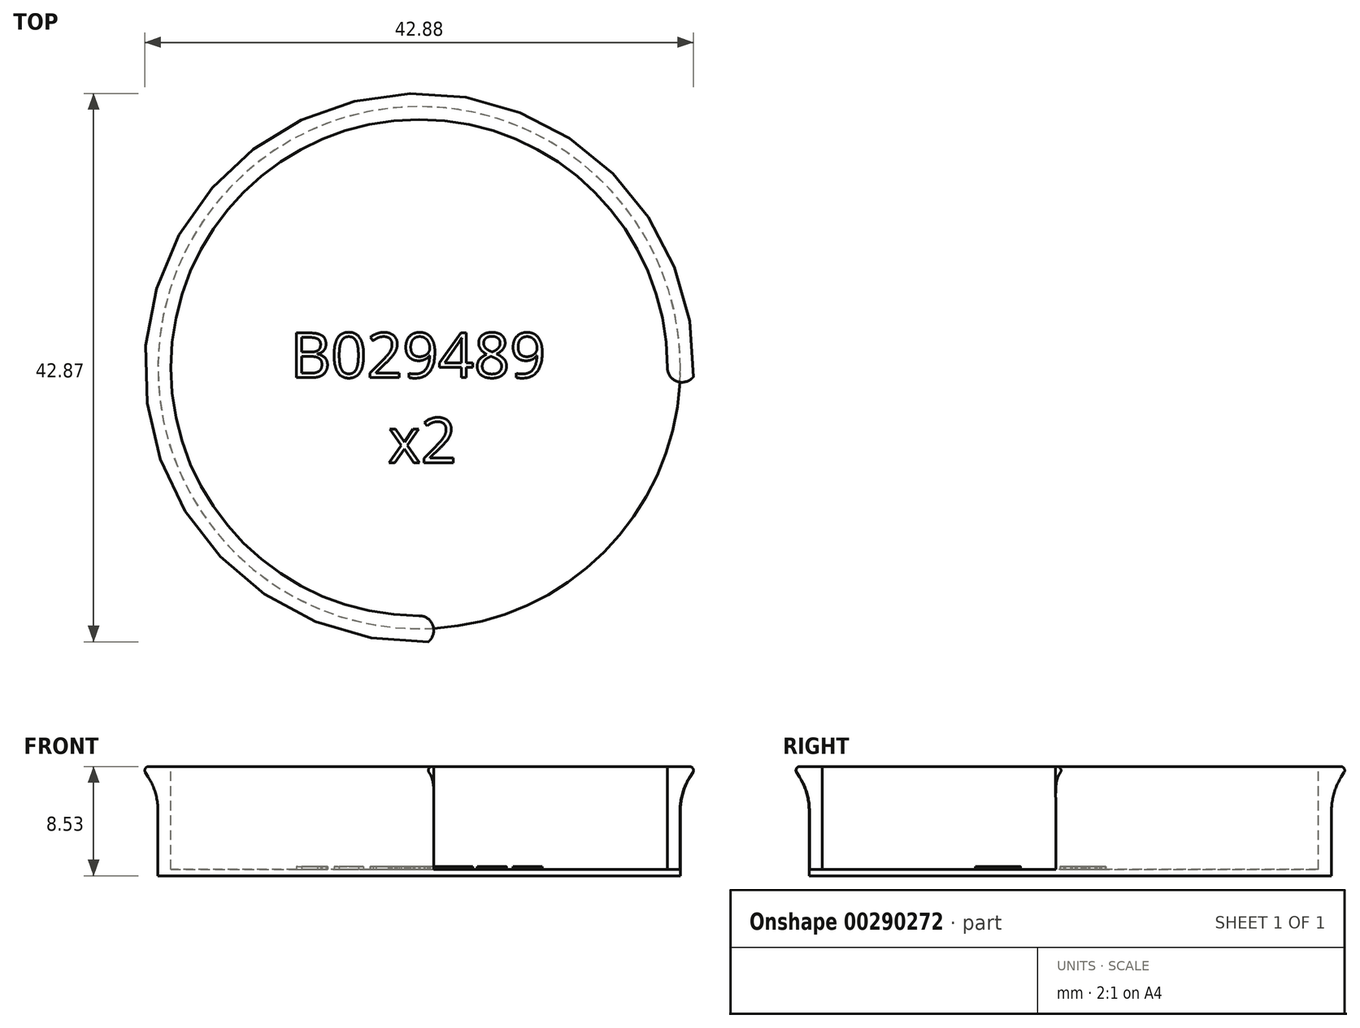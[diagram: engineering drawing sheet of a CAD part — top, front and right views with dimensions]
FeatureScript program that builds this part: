
annotation { "Feature Type Name" : "Feature", "Feature Type Description" : "" }
export const myFeature = defineFeature(function(context is Context, id is Id, definition is map)
    precondition{}
    {
        {
            var Q0;
            Q0=qCreatedBy(makeId("Right.planeOp"),FACE);
            var sketch = newSketch(context, id + "F0", { "sketchPlane" : qUnion([Q0])});
            skLineSegment(sketch, "E0", {"start": v(5.75, 8.53) * mm, "end": v(5.75, 0) * mm});
            skLineSegment(sketch, "E1", {"start": v(5.75, 8.53) * mm, "end": v(-15.93, 8.53) * mm});
            skLineSegment(sketch, "E2", {"start": v(5.75, 0) * mm, "end": v(-14.66, 0) * mm});
            skLineSegment(sketch, "E3", {"start": v(-14.66, 0) * mm, "end": v(-14.66, 6.5) * mm});
            skLineSegment(sketch, "E4", {"start": v(-14.66, 6.5) * mm, "end": v(-14.66, 8.53) * mm});
            skLineSegment(sketch, "E5", {"start": v(-15.93, 8.53) * mm, "end": v(-14.66, 6.5) * mm});
            skSolve(sketch);
        }
        {
            var Q0;
            Q0=qSketchRegion(id+"F0",true);
            var Q1;
            Q1=sQuery(id+"F0.wireOp",EDGE,"E0");
            revolve(context, id + "F1", {"entities" : qUnion([Q0]), "axis" : qUnion([Q1]), "revolveType" : RevolveType.FULL});
        }
        {
            var Q0;
            Q0=makeQuery(id+"F1.opRevolve","SWEPT_FACE",FACE,{"disambiguationData":[OSD([sQuery(id+"F0.wireOp",EDGE,"E1")])]});
            var sketch = newSketch(context, id + "F2", { "sketchPlane" : qUnion([Q0])});
            skCircle(sketch, "E6", {"center": v(0, 5.75) * mm, "radius": 19.4 * mm});
            skLineSegment(sketch, "E7.bottom", {"start": v(0, 5.75) * mm, "end": v(21.68, 5.75) * mm});
            skLineSegment(sketch, "E7.top", {"start": v(0, -15.93) * mm, "end": v(21.68, -15.93) * mm});
            skLineSegment(sketch, "E7.left", {"start": v(0, 5.75) * mm, "end": v(0, -15.93) * mm});
            skLineSegment(sketch, "E7.right", {"start": v(21.68, 5.75) * mm, "end": v(21.68, -15.93) * mm});
            skArc(sketch, "E8", {"start": v(0, -15.93) * mm, "mid": v(1.14, -14.78) * mm, "end": v(0, -13.64) * mm});
            skArc(sketch, "E9", {"start": v(19.4, 5.75) * mm, "mid": v(20.54, 4.61) * mm, "end": v(21.68, 5.75) * mm});
            skSolve(sketch);
        }
        {
            var Q0;
            {var subQ0=sQuery(id+"F2.wireOp",EDGE,"E7.left");var subQ3=sQuery(id+"F2.wireOp",EDGE,"E7.bottom");var subQ5=makeQuery(id+"F2.imprint","INTERSECT",VERTEX,{"derivedFrom":[subQ3,subQ0]});Q0=makeQuery(id+"F2.imprint","IMPRINT",FACE,{"disambiguationData":[TD([[makeQuery(id+"F2.imprint","IMPRINT",EDGE,{"disambiguationData":[TD([[subQ5,-1.0]])],"derivedFrom":subQ3}),1.0]])]});}
            var Q1;
            {var subQ0=sQuery(id+"F2.wireOp",EDGE,"E7.left");var subQ3=sQuery(id+"F2.wireOp",EDGE,"E7.bottom");var subQ5=makeQuery(id+"F2.imprint","INTERSECT",VERTEX,{"derivedFrom":[subQ3,subQ0]});Q1=makeQuery(id+"F2.imprint","IMPRINT",FACE,{"disambiguationData":[TD([[makeQuery(id+"F2.imprint","IMPRINT",EDGE,{"disambiguationData":[TD([[subQ5,-1.0]])],"derivedFrom":subQ3}),-1.0]])]});}
            var Q2;
            {var subQ0=sQuery(id+"F2.wireOp",EDGE,"E8");Q2=makeQuery(id+"F2.imprint","IMPRINT",FACE,{"disambiguationData":[TD([[makeQuery(id+"F2.imprint","IMPRINT",EDGE,{"derivedFrom":subQ0}),-1.0]])]});}
            extrude(context, id + "F3", {"entities" : qUnion([Q0, Q1, Q2]), "operationType" : NewBodyOperationType.REMOVE, "oppositeDirection" : true, "depth" : 8.03 * mm});
        }
        {
            var Q0;
            Q0=makeQuery(id+"F1.opRevolve","SWEPT_EDGE",EDGE,{"disambiguationData":[OSD([sQuery(id+"F0.wireOp",EDGE,"E1"),sQuery(id+"F0.wireOp",EDGE,"E5")])]});
            var Q1;
            Q1=makeQuery(id+"F3.boolean.opBoolean","COPY",EDGE,{"derivedFrom":makeQuery(id+"F3.opExtrude","CAP_EDGE",EDGE,{"disambiguationData":[OSD([sQuery(id+"F2.wireOp",EDGE,"E6")])],"isStart":true})});
            fillet(context, id + "F4", {"entities" : qUnion([Q0, Q1]), "radius" : 0.3 * mm, "tangentPropagation" : true, "allowEdgeOverflow" : false});
        }
        {
            var Q0;
            Q0=makeQuery(id+"F1.opRevolve","SWEPT_EDGE",EDGE,{"disambiguationData":[OSD([sQuery(id+"F0.wireOp",EDGE,"E3"),sQuery(id+"F0.wireOp",EDGE,"E4"),sQuery(id+"F0.wireOp",EDGE,"E5")])]});
            fillet(context, id + "F5", {"entities" : qUnion([Q0]), "radius" : 5 * mm, "tangentPropagation" : true, "allowEdgeOverflow" : false});
        }
        {
            var Q0;
            Q0=makeQuery(id+"F3.boolean.opBoolean","COPY",FACE,{"derivedFrom":makeQuery(id+"F3.opExtrude","CAP_FACE",FACE,{"disambiguationData":[OSD([sQuery(id+"F0.wireOp",EDGE,"E1"),sQuery(id+"F0.wireOp",EDGE,"E5"),sQuery(id+"F2.wireOp",EDGE,"E6"),sQuery(id+"F2.wireOp",EDGE,"E8"),sQuery(id+"F2.wireOp",EDGE,"E9")])],"isStart":false})});
            var sketch = newSketch(context, id + "F6", { "sketchPlane" : qUnion([Q0])});
            skText(sketch, "E10", { "text": "B029489\n      x2", "fontName": "OpenSans-Regular.ttf"});
            const initialGuessF6  = {"E10": [-0.01006, 0.00498, 1, 0, 0.00352]};
            skSetInitialGuess(sketch, initialGuessF6);
            skSolve(sketch);
        }
        {
            var Q0;
            Q0=qSketchRegion(id+"F6",true);
            extrude(context, id + "F7", {"entities" : qUnion([Q0]), "operationType" : NewBodyOperationType.ADD, "depth" : 0.2 * mm});
        }
    });
